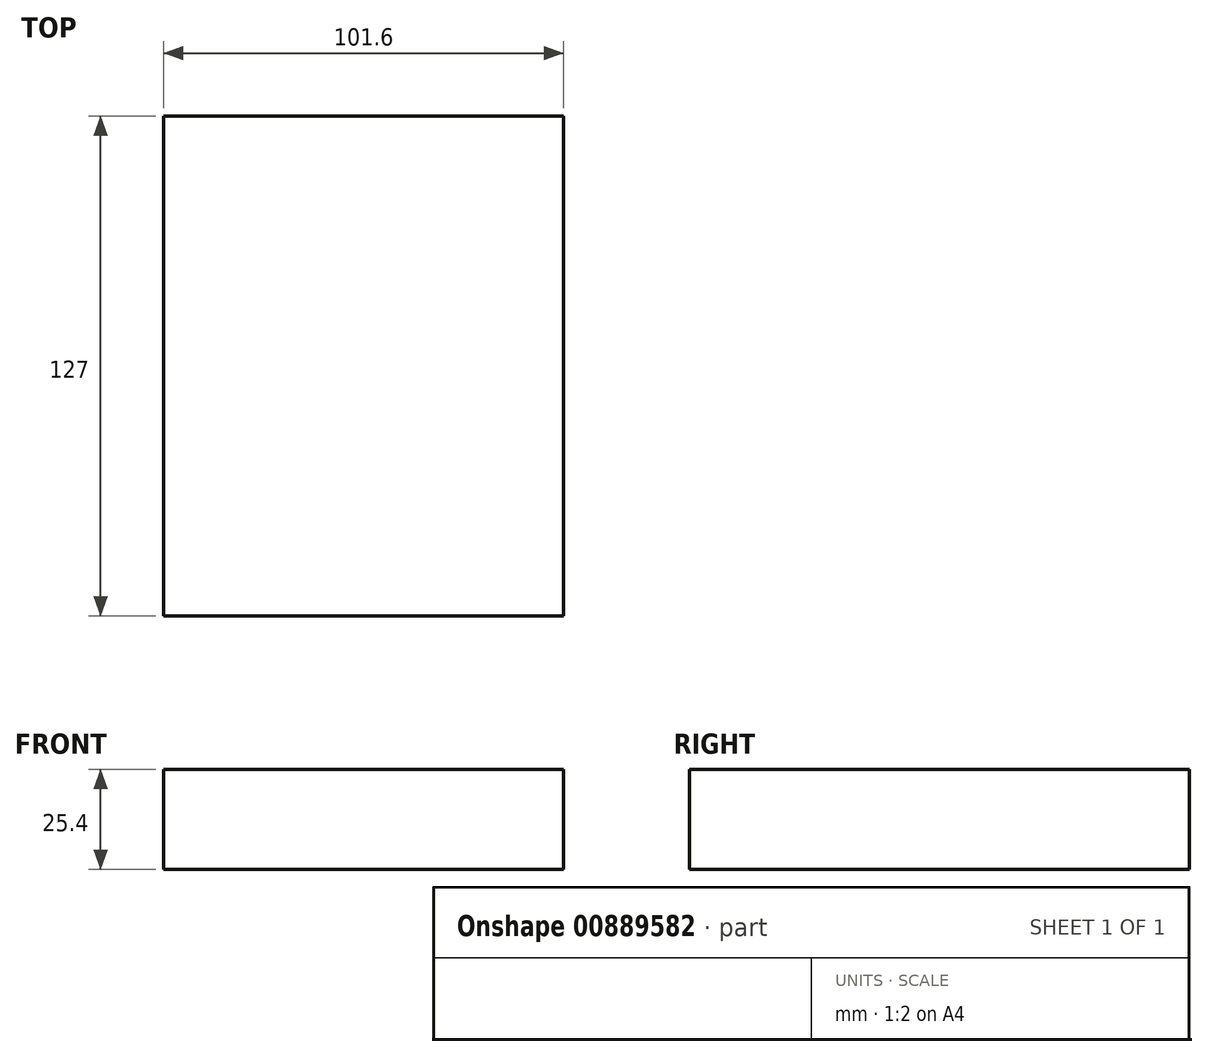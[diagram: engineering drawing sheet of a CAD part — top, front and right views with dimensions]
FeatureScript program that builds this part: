
annotation { "Feature Type Name" : "Feature", "Feature Type Description" : "" }
export const myFeature = defineFeature(function(context is Context, id is Id, definition is map)
    precondition{}
    {
        {
            var Q0;
            Q0=qCreatedBy(makeId("Top.planeOp"),FACE);
            var sketch = newSketch(context, id + "F0", { "sketchPlane" : qUnion([Q0])});
            skLineSegment(sketch, "E0.bottom", {"start": v(-50.8, 76.2) * mm, "end": v(50.8, 76.2) * mm});
            skLineSegment(sketch, "E0.top", {"start": v(-50.8, -50.8) * mm, "end": v(50.8, -50.8) * mm});
            skLineSegment(sketch, "E0.left", {"start": v(-50.8, 76.2) * mm, "end": v(-50.8, -50.8) * mm});
            skLineSegment(sketch, "E0.right", {"start": v(50.8, 76.2) * mm, "end": v(50.8, -50.8) * mm});
            skSolve(sketch);
        }
        {
            var Q0;
            Q0=makeQuery(id+"F0.imprint","IMPRINT",FACE,{"disambiguationData":[TD([[makeQuery(id+"F0.imprint","IMPRINT",EDGE,{"derivedFrom":sQuery(id+"F0.wireOp",EDGE,"E0.bottom")}),-1.0]])]});
            extrude(context, id + "F1", {"entities" : qUnion([Q0]), "depth" : 25.4 * mm, "offsetDistance" : 25.4 * mm});
        }
    });
